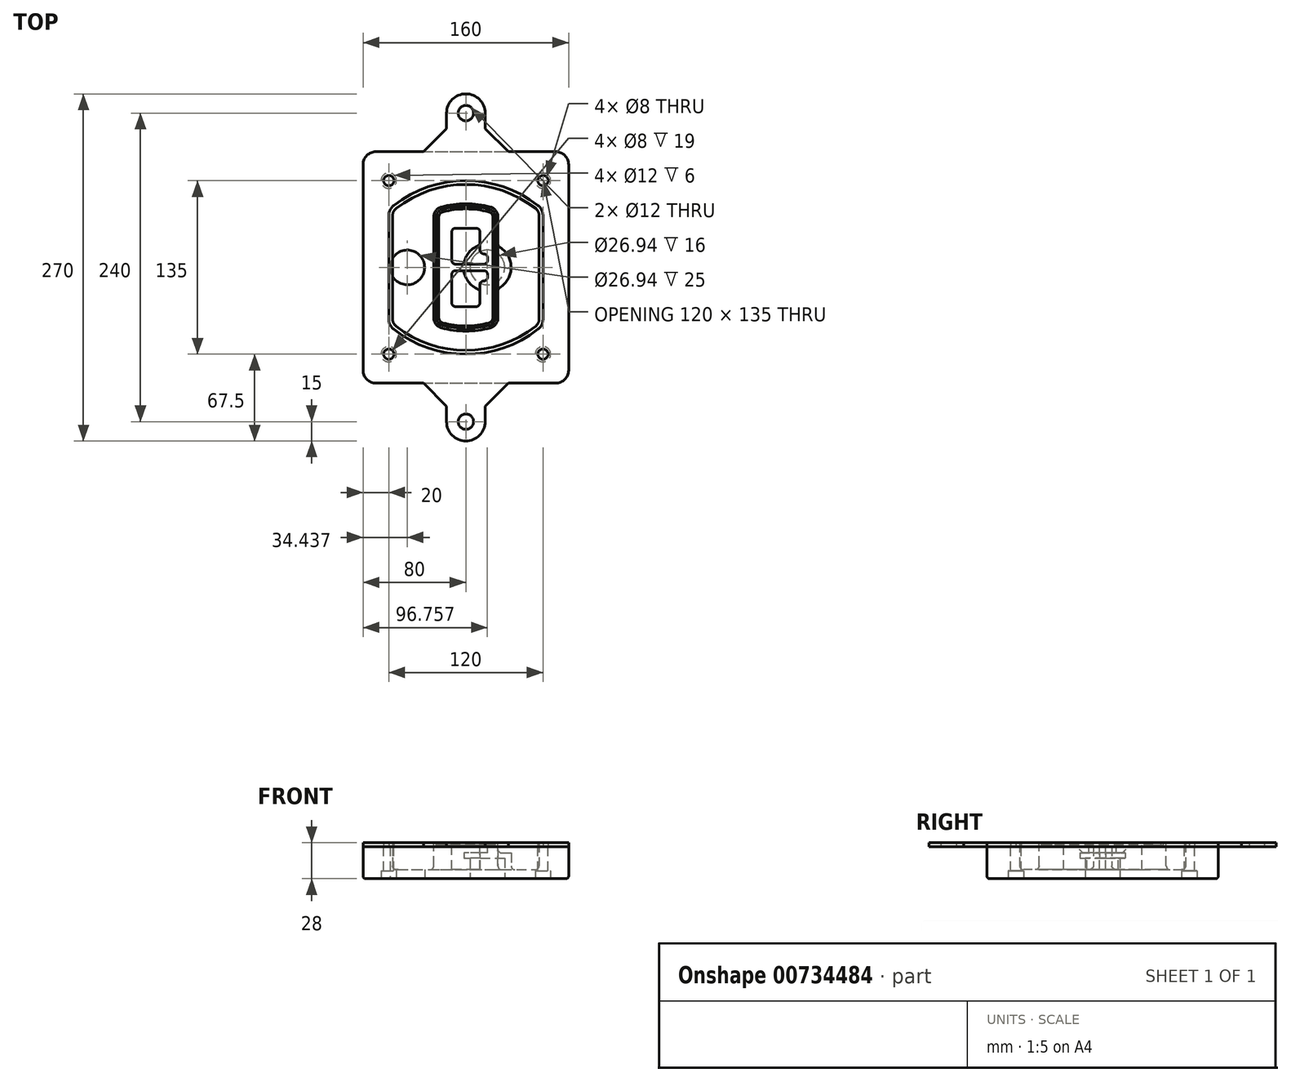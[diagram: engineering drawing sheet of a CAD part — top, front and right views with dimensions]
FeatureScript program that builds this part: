
annotation { "Feature Type Name" : "Feature", "Feature Type Description" : "" }
export const myFeature = defineFeature(function(context is Context, id is Id, definition is map)
    precondition{}
    {
        {
            var Q0;
            Q0=qCreatedBy(makeId("Top.planeOp"),FACE);
            var sketch = newSketch(context, id + "F0", { "sketchPlane" : qUnion([Q0])});
            skPoint(sketch, "E0.rect.middle", {"position": v(0, 0) * mm});
            skLineSegment(sketch, "E1.bottom", {"start": v(-70, -90) * mm, "end": v(70, -90) * mm});
            skLineSegment(sketch, "E1.top", {"start": v(-70, 90) * mm, "end": v(70, 90) * mm});
            skLineSegment(sketch, "E1.left", {"start": v(-80, -80) * mm, "end": v(-80, 80) * mm});
            skLineSegment(sketch, "E1.right", {"start": v(80, -80) * mm, "end": v(80, 80) * mm});
            skLineSegment(sketch, "E2", {"start": v(-80, 90) * mm, "end": v(80, -90) * mm, "construction": true});
            skLineSegment(sketch, "E3", {"start": v(80, 90) * mm, "end": v(-80, -90) * mm, "construction": true});
            skCircle(sketch, "E4", {"center": v(-60, 67.5) * mm, "radius": 4 * mm});
            skCircle(sketch, "E5", {"center": v(60, 67.5) * mm, "radius": 4 * mm});
            skCircle(sketch, "E6", {"center": v(60, -67.5) * mm, "radius": 4 * mm});
            skCircle(sketch, "E7", {"center": v(-60, -67.5) * mm, "radius": 4 * mm});
            skLineSegment(sketch, "E8", {"start": v(-60, 67.5) * mm, "end": v(60, 67.5) * mm, "construction": true});
            skLineSegment(sketch, "E9", {"start": v(60, 67.5) * mm, "end": v(60, -67.5) * mm, "construction": true});
            skLineSegment(sketch, "E10", {"start": v(60, -67.5) * mm, "end": v(-60, -67.5) * mm, "construction": true});
            skLineSegment(sketch, "E11", {"start": v(-60, -67.5) * mm, "end": v(-60, 67.5) * mm, "construction": true});
            skLineSegment(sketch, "E12", {"start": v(-60, 40.3) * mm, "end": v(-60, -40.3) * mm});
            skLineSegment(sketch, "E13", {"start": v(60, 40.3) * mm, "end": v(60, -40.3) * mm});
            skArc(sketch, "E14", {"start": v(56.15, 48.18) * mm, "mid": v(0, 67.5) * mm, "end": v(-56.15, 48.18) * mm});
            skArc(sketch, "E15", {"start": v(-56.15, -48.18) * mm, "mid": v(0, -67.5) * mm, "end": v(56.15, -48.18) * mm});
            skLineSegment(sketch, "E16", {"start": v(-60, 0) * mm, "end": v(60, 0) * mm, "construction": true});
            skPoint(sketch, "E17.visualSharp", {"position": v(-60, -45) * mm});
            skArc(sketch, "E17.filletArc", {"start": v(-60, -40.3) * mm, "mid": v(-58.99, -44.68) * mm, "end": v(-56.15, -48.18) * mm});
            skPoint(sketch, "E18.visualSharp", {"position": v(-60, 45) * mm});
            skArc(sketch, "E18.filletArc", {"start": v(-56.15, 48.18) * mm, "mid": v(-58.99, 44.68) * mm, "end": v(-60, 40.3) * mm});
            skPoint(sketch, "E19.visualSharp", {"position": v(60, 45) * mm});
            skArc(sketch, "E19.filletArc", {"start": v(60, 40.3) * mm, "mid": v(58.99, 44.68) * mm, "end": v(56.15, 48.18) * mm});
            skPoint(sketch, "E20.visualSharp", {"position": v(60, -45) * mm});
            skArc(sketch, "E20.filletArc", {"start": v(56.15, -48.18) * mm, "mid": v(58.99, -44.68) * mm, "end": v(60, -40.3) * mm});
            skPoint(sketch, "E21.visualSharp", {"position": v(-80, 90) * mm});
            skArc(sketch, "E21.filletArc", {"start": v(-70, 90) * mm, "mid": v(-77.07, 87.07) * mm, "end": v(-80, 80) * mm});
            skPoint(sketch, "E22.visualSharp", {"position": v(80, 90) * mm});
            skArc(sketch, "E22.filletArc", {"start": v(80, 80) * mm, "mid": v(77.07, 87.07) * mm, "end": v(70, 90) * mm});
            skPoint(sketch, "E23.visualSharp", {"position": v(80, -90) * mm});
            skArc(sketch, "E23.filletArc", {"start": v(70, -90) * mm, "mid": v(77.07, -87.07) * mm, "end": v(80, -80) * mm});
            skPoint(sketch, "E24.visualSharp", {"position": v(-80, -90) * mm});
            skArc(sketch, "E24.filletArc", {"start": v(-80, -80) * mm, "mid": v(-77.07, -87.07) * mm, "end": v(-70, -90) * mm});
            skArc(sketch, "E25.0", {"start": v(57, 40.3) * mm, "mid": v(56.3, 43.36) * mm, "end": v(54.3, 45.81) * mm});
            skLineSegment(sketch, "E25.1", {"start": v(57, 40.3) * mm, "end": v(57, -40.3) * mm});
            skArc(sketch, "E25.2", {"start": v(54.3, -45.81) * mm, "mid": v(56.3, -43.36) * mm, "end": v(57, -40.3) * mm});
            skArc(sketch, "E25.3", {"start": v(-54.3, -45.81) * mm, "mid": v(0, -64.5) * mm, "end": v(54.3, -45.81) * mm});
            skArc(sketch, "E25.4", {"start": v(-57, -40.3) * mm, "mid": v(-56.3, -43.36) * mm, "end": v(-54.3, -45.81) * mm});
            skArc(sketch, "E25.5", {"start": v(54.3, 45.81) * mm, "mid": v(0, 64.5) * mm, "end": v(-54.3, 45.81) * mm});
            skLineSegment(sketch, "E25.6", {"start": v(-57, 40.3) * mm, "end": v(-57, -40.3) * mm});
            skArc(sketch, "E25.7", {"start": v(-54.3, 45.81) * mm, "mid": v(-56.3, 43.36) * mm, "end": v(-57, 40.3) * mm});
            skArc(sketch, "E26.0", {"start": v(-58.62, 51.33) * mm, "mid": v(-62.58, 46.43) * mm, "end": v(-64, 40.3) * mm});
            skArc(sketch, "E26.1", {"start": v(58.62, 51.33) * mm, "mid": v(0, 71.5) * mm, "end": v(-58.62, 51.33) * mm});
            skArc(sketch, "E26.2", {"start": v(64, 40.3) * mm, "mid": v(62.58, 46.43) * mm, "end": v(58.62, 51.33) * mm});
            skLineSegment(sketch, "E26.3", {"start": v(64, 40.3) * mm, "end": v(64, -40.3) * mm});
            skArc(sketch, "E26.4", {"start": v(58.62, -51.33) * mm, "mid": v(62.58, -46.43) * mm, "end": v(64, -40.3) * mm});
            skLineSegment(sketch, "E26.5", {"start": v(-64, 40.3) * mm, "end": v(-64, -40.3) * mm});
            skArc(sketch, "E26.6", {"start": v(-58.62, -51.33) * mm, "mid": v(0, -71.5) * mm, "end": v(58.62, -51.33) * mm});
            skArc(sketch, "E26.7", {"start": v(-64, -40.3) * mm, "mid": v(-62.58, -46.43) * mm, "end": v(-58.62, -51.33) * mm});
            skSolve(sketch);
        }
        {
            var Q0;
            Q0=makeQuery(id+"F0.imprint","IMPRINT",FACE,{"disambiguationData":[TD([[makeQuery(id+"F0.imprint","IMPRINT",EDGE,{"derivedFrom":sQuery(id+"F0.wireOp",EDGE,"E1.bottom")}),1.0]])]});
            var Q1;
            Q1=makeQuery(id+"F0.imprint","IMPRINT",FACE,{"disambiguationData":[TD([[makeQuery(id+"F0.imprint","IMPRINT",EDGE,{"derivedFrom":sQuery(id+"F0.wireOp",EDGE,"E12")}),1.0]])]});
            var Q2;
            Q2=makeQuery(id+"F0.imprint","IMPRINT",FACE,{"disambiguationData":[TD([[makeQuery(id+"F0.imprint","IMPRINT",EDGE,{"derivedFrom":sQuery(id+"F0.wireOp",EDGE,"E25.0")}),1.0]])]});
            var Q3;
            Q3=makeQuery(id+"F0.imprint","IMPRINT",FACE,{"disambiguationData":[TD([[makeQuery(id+"F0.imprint","IMPRINT",EDGE,{"derivedFrom":sQuery(id+"F0.wireOp",EDGE,"E12")}),-1.0]])]});
            extrude(context, id + "F1", {"entities" : qUnion([Q0, Q1, Q2, Q3]), "oppositeDirection" : true, "depth" : 25 * mm});
        }
        {
            var Q0;
            Q0=makeQuery(id+"F0.imprint","IMPRINT",FACE,{"disambiguationData":[TD([[makeQuery(id+"F0.imprint","IMPRINT",EDGE,{"derivedFrom":sQuery(id+"F0.wireOp",EDGE,"E12")}),1.0]])]});
            extrude(context, id + "F2", {"entities" : qUnion([Q0]), "operationType" : NewBodyOperationType.ADD, "depth" : 3 * mm});
        }
        {
            var Q0;
            Q0=makeQuery(id+"F0.imprint","IMPRINT",FACE,{"disambiguationData":[TD([[makeQuery(id+"F0.imprint","IMPRINT",EDGE,{"derivedFrom":sQuery(id+"F0.wireOp",EDGE,"E25.0")}),1.0]])]});
            extrude(context, id + "F3", {"entities" : qUnion([Q0]), "operationType" : NewBodyOperationType.REMOVE, "oppositeDirection" : true, "depth" : 18 * mm});
        }
        {
            var Q0;
            Q0=makeQuery(id+"F2.opExtrude","CAP_FACE",FACE,{"disambiguationData":[OSD([sQuery(id+"F0.wireOp",EDGE,"E12"),sQuery(id+"F0.wireOp",EDGE,"E13"),sQuery(id+"F0.wireOp",EDGE,"E14"),sQuery(id+"F0.wireOp",EDGE,"E15"),sQuery(id+"F0.wireOp",EDGE,"E17.filletArc"),sQuery(id+"F0.wireOp",EDGE,"E18.filletArc"),sQuery(id+"F0.wireOp",EDGE,"E19.filletArc"),sQuery(id+"F0.wireOp",EDGE,"E20.filletArc"),sQuery(id+"F0.wireOp",EDGE,"E25.0"),sQuery(id+"F0.wireOp",EDGE,"E25.1"),sQuery(id+"F0.wireOp",EDGE,"E25.2"),sQuery(id+"F0.wireOp",EDGE,"E25.3"),sQuery(id+"F0.wireOp",EDGE,"E25.4"),sQuery(id+"F0.wireOp",EDGE,"E25.5"),sQuery(id+"F0.wireOp",EDGE,"E25.6"),sQuery(id+"F0.wireOp",EDGE,"E25.7")])],"isStart":false});
            var sketch = newSketch(context, id + "F4", { "sketchPlane" : qUnion([Q0])});
            skArc(sketch, "E27.0", {"start": v(-19.08, -46.97) * mm, "mid": v(0, -49.5) * mm, "end": v(19.08, -46.97) * mm});
            skArc(sketch, "E28.0", {"start": v(19.08, 46.97) * mm, "mid": v(0, 49.5) * mm, "end": v(-19.08, 46.97) * mm});
            skLineSegment(sketch, "E29", {"start": v(-25, 39.25) * mm, "end": v(-25, -39.25) * mm});
            skLineSegment(sketch, "E30", {"start": v(25, 39.25) * mm, "end": v(25, -39.25) * mm});
            skLineSegment(sketch, "E31", {"start": v(-25, 45.1) * mm, "end": v(25, 45.1) * mm, "construction": true});
            skLineSegment(sketch, "E32", {"start": v(-25, -45.1) * mm, "end": v(25, -45.1) * mm, "construction": true});
            skPoint(sketch, "E33.visualSharp", {"position": v(-25, 45.1) * mm});
            skArc(sketch, "E33.filletArc", {"start": v(-19.08, 46.97) * mm, "mid": v(-23.35, 44.11) * mm, "end": v(-25, 39.25) * mm});
            skPoint(sketch, "E34.visualSharp", {"position": v(25, 45.1) * mm});
            skArc(sketch, "E34.filletArc", {"start": v(25, 39.25) * mm, "mid": v(23.35, 44.11) * mm, "end": v(19.08, 46.97) * mm});
            skPoint(sketch, "E35.visualSharp", {"position": v(25, -45.1) * mm});
            skArc(sketch, "E35.filletArc", {"start": v(19.08, -46.97) * mm, "mid": v(23.35, -44.11) * mm, "end": v(25, -39.25) * mm});
            skPoint(sketch, "E36.visualSharp", {"position": v(-25, -45.1) * mm});
            skArc(sketch, "E36.filletArc", {"start": v(-25, -39.25) * mm, "mid": v(-23.35, -44.11) * mm, "end": v(-19.08, -46.97) * mm});
            skArc(sketch, "E37.0", {"start": v(54.3, 45.81) * mm, "mid": v(0, 64.5) * mm, "end": v(-54.3, 45.81) * mm});
            skArc(sketch, "E37.1", {"start": v(-54.3, 45.81) * mm, "mid": v(-56.3, 43.36) * mm, "end": v(-57, 40.3) * mm});
            skLineSegment(sketch, "E37.2", {"start": v(-57, 40.3) * mm, "end": v(-57, -40.3) * mm});
            skArc(sketch, "E37.3", {"start": v(-57, -40.3) * mm, "mid": v(-56.3, -43.36) * mm, "end": v(-54.3, -45.81) * mm});
            skArc(sketch, "E37.4", {"start": v(-54.3, -45.81) * mm, "mid": v(0, -64.5) * mm, "end": v(54.3, -45.81) * mm});
            skArc(sketch, "E37.5", {"start": v(54.3, -45.81) * mm, "mid": v(56.3, -43.36) * mm, "end": v(57, -40.3) * mm});
            skLineSegment(sketch, "E37.6", {"start": v(57, 40.3) * mm, "end": v(57, -40.3) * mm});
            skArc(sketch, "E37.7", {"start": v(57, 40.3) * mm, "mid": v(56.3, 43.36) * mm, "end": v(54.3, 45.81) * mm});
            skLineSegment(sketch, "E38.0", {"start": v(23, 39.25) * mm, "end": v(23, -39.25) * mm});
            skArc(sketch, "E38.1", {"start": v(18.56, -45.04) * mm, "mid": v(21.76, -42.9) * mm, "end": v(23, -39.25) * mm});
            skArc(sketch, "E38.2", {"start": v(-18.56, -45.04) * mm, "mid": v(0, -47.5) * mm, "end": v(18.56, -45.04) * mm});
            skArc(sketch, "E38.3", {"start": v(-23, -39.25) * mm, "mid": v(-21.76, -42.9) * mm, "end": v(-18.56, -45.04) * mm});
            skLineSegment(sketch, "E38.4", {"start": v(-23, 39.25) * mm, "end": v(-23, -39.25) * mm});
            skArc(sketch, "E38.5", {"start": v(23, 39.25) * mm, "mid": v(21.76, 42.9) * mm, "end": v(18.56, 45.04) * mm});
            skArc(sketch, "E38.6", {"start": v(-18.56, 45.04) * mm, "mid": v(-21.76, 42.9) * mm, "end": v(-23, 39.25) * mm});
            skArc(sketch, "E38.7", {"start": v(18.56, 45.04) * mm, "mid": v(0, 47.5) * mm, "end": v(-18.56, 45.04) * mm});
            skArc(sketch, "E39.0", {"start": v(21, 39.25) * mm, "mid": v(20.18, 41.68) * mm, "end": v(18.04, 43.1) * mm});
            skLineSegment(sketch, "E39.1", {"start": v(21, 39.25) * mm, "end": v(21, -39.25) * mm});
            skArc(sketch, "E39.2", {"start": v(18.04, -43.1) * mm, "mid": v(20.18, -41.68) * mm, "end": v(21, -39.25) * mm});
            skArc(sketch, "E39.3", {"start": v(-18.04, -43.1) * mm, "mid": v(0, -45.5) * mm, "end": v(18.04, -43.1) * mm});
            skArc(sketch, "E39.4", {"start": v(-21, -39.25) * mm, "mid": v(-20.18, -41.68) * mm, "end": v(-18.04, -43.1) * mm});
            skArc(sketch, "E39.5", {"start": v(18.04, 43.1) * mm, "mid": v(0, 45.5) * mm, "end": v(-18.04, 43.1) * mm});
            skLineSegment(sketch, "E39.6", {"start": v(-21, 39.25) * mm, "end": v(-21, -39.25) * mm});
            skArc(sketch, "E39.7", {"start": v(-18.04, 43.1) * mm, "mid": v(-20.18, 41.68) * mm, "end": v(-21, 39.25) * mm});
            skLineSegment(sketch, "E40", {"start": v(-25, 0) * mm, "end": v(25, 0) * mm, "construction": true});
            skLineSegment(sketch, "E41", {"start": v(-11, 5.5) * mm, "end": v(-11, 27.5) * mm});
            skLineSegment(sketch, "E42", {"start": v(-8, 30.5) * mm, "end": v(8, 30.5) * mm});
            skLineSegment(sketch, "E43", {"start": v(11, 27.5) * mm, "end": v(11, 13.5) * mm});
            skLineSegment(sketch, "E44", {"start": v(14, 10.5) * mm, "end": v(14, 10.5) * mm});
            skLineSegment(sketch, "E45", {"start": v(17, 7.5) * mm, "end": v(17, 5.5) * mm});
            skLineSegment(sketch, "E46", {"start": v(14, 2.5) * mm, "end": v(-8, 2.5) * mm});
            skPoint(sketch, "E47.visualSharp", {"position": v(-11, 30.5) * mm});
            skArc(sketch, "E47.filletArc", {"start": v(-8, 30.5) * mm, "mid": v(-10.12, 29.62) * mm, "end": v(-11, 27.5) * mm});
            skPoint(sketch, "E48.visualSharp", {"position": v(11, 30.5) * mm});
            skArc(sketch, "E48.filletArc", {"start": v(11, 27.5) * mm, "mid": v(10.12, 29.62) * mm, "end": v(8, 30.5) * mm});
            skPoint(sketch, "E49.visualSharp", {"position": v(11, 10.5) * mm});
            skArc(sketch, "E49.filletArc", {"start": v(11, 13.5) * mm, "mid": v(11.88, 11.38) * mm, "end": v(14, 10.5) * mm});
            skPoint(sketch, "E50.visualSharp", {"position": v(17, 10.5) * mm});
            skArc(sketch, "E50.filletArc", {"start": v(17, 7.5) * mm, "mid": v(16.12, 9.62) * mm, "end": v(14, 10.5) * mm});
            skPoint(sketch, "E51.visualSharp", {"position": v(17, 2.5) * mm});
            skArc(sketch, "E51.filletArc", {"start": v(14, 2.5) * mm, "mid": v(16.12, 3.38) * mm, "end": v(17, 5.5) * mm});
            skPoint(sketch, "E52.visualSharp", {"position": v(-11, 2.5) * mm});
            skArc(sketch, "E52.filletArc", {"start": v(-11, 5.5) * mm, "mid": v(-10.12, 3.38) * mm, "end": v(-8, 2.5) * mm});
            skLineSegment(sketch, "E53.0.MirrorCS", {"start": v(14, -2.5) * mm, "end": v(-8, -2.5) * mm});
            skArc(sketch, "E54.0.MirrorCS", {"start": v(-11, -5.5) * mm, "mid": v(-10.12, -3.38) * mm, "end": v(-8, -2.5) * mm});
            skLineSegment(sketch, "E55.0.MirrorCS", {"start": v(-11, -5.5) * mm, "end": v(-11, -27.5) * mm});
            skArc(sketch, "E56.0.MirrorCS", {"start": v(-8, -30.5) * mm, "mid": v(-10.12, -29.62) * mm, "end": v(-11, -27.5) * mm});
            skLineSegment(sketch, "E57.0.MirrorCS", {"start": v(-8, -30.5) * mm, "end": v(8, -30.5) * mm});
            skArc(sketch, "E58.0.MirrorCS", {"start": v(11, -27.5) * mm, "mid": v(10.12, -29.62) * mm, "end": v(8, -30.5) * mm});
            skLineSegment(sketch, "E59.0.MirrorCS", {"start": v(11, -27.5) * mm, "end": v(11, -13.5) * mm});
            skArc(sketch, "E60.0.MirrorCS", {"start": v(11, -13.5) * mm, "mid": v(11.88, -11.38) * mm, "end": v(14, -10.5) * mm});
            skArc(sketch, "E61.0.MirrorCS", {"start": v(17, -7.5) * mm, "mid": v(16.12, -9.62) * mm, "end": v(14, -10.5) * mm});
            skLineSegment(sketch, "E62.0.MirrorCS", {"start": v(17, -7.5) * mm, "end": v(17, -5.5) * mm});
            skArc(sketch, "E63.0.MirrorCS", {"start": v(14, -2.5) * mm, "mid": v(16.12, -3.38) * mm, "end": v(17, -5.5) * mm});
            skSolve(sketch);
        }
        {
            var Q0;
            Q0=makeQuery(id+"F4.imprint","IMPRINT",FACE,{"disambiguationData":[TD([[makeQuery(id+"F4.imprint","IMPRINT",EDGE,{"derivedFrom":sQuery(id+"F4.wireOp",EDGE,"E27.0")}),1.0]])]});
            var Q1;
            Q1=makeQuery(id+"F4.imprint","IMPRINT",FACE,{"disambiguationData":[TD([[makeQuery(id+"F4.imprint","IMPRINT",EDGE,{"derivedFrom":sQuery(id+"F4.wireOp",EDGE,"E38.0")}),-1.0]])]});
            var Q2;
            Q2=makeQuery(id+"F4.imprint","IMPRINT",FACE,{"disambiguationData":[TD([[makeQuery(id+"F4.imprint","IMPRINT",EDGE,{"derivedFrom":sQuery(id+"F4.wireOp",EDGE,"E39.0")}),1.0]])]});
            extrude(context, id + "F5", {"entities" : qUnion([Q0, Q1, Q2]), "operationType" : NewBodyOperationType.ADD, "endBound" : BoundingType.UP_TO_NEXT, "oppositeDirection" : true, "depth" : 25 * mm});
        }
        {
            var Q0;
            Q0=makeQuery(id+"F4.imprint","IMPRINT",FACE,{"disambiguationData":[TD([[makeQuery(id+"F4.imprint","IMPRINT",EDGE,{"derivedFrom":sQuery(id+"F4.wireOp",EDGE,"E38.0")}),-1.0]])]});
            extrude(context, id + "F6", {"entities" : qUnion([Q0]), "operationType" : NewBodyOperationType.REMOVE, "oppositeDirection" : true, "depth" : 2 * mm});
        }
        {
            var Q0;
            Q0=makeQuery(id+"F1.opExtrude","CAP_FACE",FACE,{"disambiguationData":[OSD([sQuery(id+"F0.wireOp",EDGE,"E1.bottom"),sQuery(id+"F0.wireOp",EDGE,"E1.top"),sQuery(id+"F0.wireOp",EDGE,"E1.left"),sQuery(id+"F0.wireOp",EDGE,"E1.right"),sQuery(id+"F0.wireOp",EDGE,"E4"),sQuery(id+"F0.wireOp",EDGE,"E5"),sQuery(id+"F0.wireOp",EDGE,"E6"),sQuery(id+"F0.wireOp",EDGE,"E7"),sQuery(id+"F0.wireOp",EDGE,"E21.filletArc"),sQuery(id+"F0.wireOp",EDGE,"E22.filletArc"),sQuery(id+"F0.wireOp",EDGE,"E23.filletArc"),sQuery(id+"F0.wireOp",EDGE,"E24.filletArc")])],"isStart":false});
            var sketch = newSketch(context, id + "F7", { "sketchPlane" : qUnion([Q0])});
            skCircle(sketch, "E64", {"center": v(16.76, 0) * mm, "radius": 13.47 * mm});
            skCircle(sketch, "E65", {"center": v(-45.56, 0) * mm, "radius": 13.47 * mm});
            skLineSegment(sketch, "E66", {"start": v(80, 0) * mm, "end": v(-80, 0) * mm});
            skCircle(sketch, "E67", {"center": v(16.76, 0) * mm, "radius": 18.47 * mm});
            skCircle(sketch, "E68", {"center": v(60, -67.5) * mm, "radius": 6 * mm});
            skCircle(sketch, "E69", {"center": v(-60, -67.5) * mm, "radius": 6 * mm});
            skCircle(sketch, "E70", {"center": v(-60, 67.5) * mm, "radius": 6 * mm});
            skCircle(sketch, "E71", {"center": v(60, 67.5) * mm, "radius": 6 * mm});
            skSolve(sketch);
        }
        {
            var Q0;
            {var subQ1=sQuery(id+"F7.wireOp",EDGE,"E66");var subQ4=sQuery(id+"F7.wireOp",EDGE,"E64");var subQ6=makeQuery(id+"F7.imprint","INTERSECT",VERTEX,{"disambiguationData":[OD(0.0)],"derivedFrom":[subQ4,subQ1]});Q0=makeQuery(id+"F7.imprint","IMPRINT",FACE,{"disambiguationData":[TD([[makeQuery(id+"F7.imprint","IMPRINT",EDGE,{"disambiguationData":[TD([[subQ6,-1.0]])],"derivedFrom":subQ4}),-1.0]])]});}
            var Q1;
            {var subQ0=sQuery(id+"F7.wireOp",EDGE,"E66");var subQ1=sQuery(id+"F7.wireOp",EDGE,"E64");var subQ3=makeQuery(id+"F7.imprint","INTERSECT",VERTEX,{"disambiguationData":[OD(0.0)],"derivedFrom":[subQ1,subQ0]});Q1=makeQuery(id+"F7.imprint","IMPRINT",FACE,{"disambiguationData":[TD([[makeQuery(id+"F7.imprint","IMPRINT",EDGE,{"disambiguationData":[TD([[subQ3,-1.0]])],"derivedFrom":subQ1}),1.0]])]});}
            var Q2;
            {var subQ0=sQuery(id+"F7.wireOp",EDGE,"E66");var subQ1=sQuery(id+"F7.wireOp",EDGE,"E64");var subQ3=makeQuery(id+"F7.imprint","INTERSECT",VERTEX,{"disambiguationData":[OD(0.0)],"derivedFrom":[subQ1,subQ0]});Q2=makeQuery(id+"F7.imprint","IMPRINT",FACE,{"disambiguationData":[TD([[makeQuery(id+"F7.imprint","IMPRINT",EDGE,{"disambiguationData":[TD([[subQ3,1.0]])],"derivedFrom":subQ1}),1.0]])]});}
            var Q3;
            {var subQ1=sQuery(id+"F7.wireOp",EDGE,"E66");var subQ4=sQuery(id+"F7.wireOp",EDGE,"E64");var subQ6=makeQuery(id+"F7.imprint","INTERSECT",VERTEX,{"disambiguationData":[OD(0.0)],"derivedFrom":[subQ4,subQ1]});Q3=makeQuery(id+"F7.imprint","IMPRINT",FACE,{"disambiguationData":[TD([[makeQuery(id+"F7.imprint","IMPRINT",EDGE,{"disambiguationData":[TD([[subQ6,1.0]])],"derivedFrom":subQ4}),-1.0]])]});}
            extrude(context, id + "F8", {"entities" : qUnion([Q0, Q1, Q2, Q3]), "operationType" : NewBodyOperationType.ADD, "oppositeDirection" : true, "depth" : 20 * mm});
        }
        {
            var Q0;
            {var subQ0=sQuery(id+"F7.wireOp",EDGE,"E66");var subQ1=sQuery(id+"F7.wireOp",EDGE,"E64");var subQ3=makeQuery(id+"F7.imprint","INTERSECT",VERTEX,{"disambiguationData":[OD(0.0)],"derivedFrom":[subQ1,subQ0]});Q0=makeQuery(id+"F7.imprint","IMPRINT",FACE,{"disambiguationData":[TD([[makeQuery(id+"F7.imprint","IMPRINT",EDGE,{"disambiguationData":[TD([[subQ3,-1.0]])],"derivedFrom":subQ1}),1.0]])]});}
            var Q1;
            {var subQ0=sQuery(id+"F7.wireOp",EDGE,"E66");var subQ1=sQuery(id+"F7.wireOp",EDGE,"E64");var subQ3=makeQuery(id+"F7.imprint","INTERSECT",VERTEX,{"disambiguationData":[OD(0.0)],"derivedFrom":[subQ1,subQ0]});Q1=makeQuery(id+"F7.imprint","IMPRINT",FACE,{"disambiguationData":[TD([[makeQuery(id+"F7.imprint","IMPRINT",EDGE,{"disambiguationData":[TD([[subQ3,1.0]])],"derivedFrom":subQ1}),1.0]])]});}
            extrude(context, id + "F9", {"entities" : qUnion([Q0, Q1]), "operationType" : NewBodyOperationType.REMOVE, "oppositeDirection" : true, "depth" : 16 * mm});
        }
        {
            var Q0;
            {var subQ0=sQuery(id+"F7.wireOp",EDGE,"E66");var subQ1=sQuery(id+"F7.wireOp",EDGE,"E65");var subQ3=makeQuery(id+"F7.imprint","INTERSECT",VERTEX,{"disambiguationData":[OD(0.0)],"derivedFrom":[subQ1,subQ0]});Q0=makeQuery(id+"F7.imprint","IMPRINT",FACE,{"disambiguationData":[TD([[makeQuery(id+"F7.imprint","IMPRINT",EDGE,{"disambiguationData":[TD([[subQ3,-1.0]])],"derivedFrom":subQ1}),1.0]])]});}
            var Q1;
            {var subQ0=sQuery(id+"F7.wireOp",EDGE,"E66");var subQ1=sQuery(id+"F7.wireOp",EDGE,"E65");var subQ3=makeQuery(id+"F7.imprint","INTERSECT",VERTEX,{"disambiguationData":[OD(0.0)],"derivedFrom":[subQ1,subQ0]});Q1=makeQuery(id+"F7.imprint","IMPRINT",FACE,{"disambiguationData":[TD([[makeQuery(id+"F7.imprint","IMPRINT",EDGE,{"disambiguationData":[TD([[subQ3,1.0]])],"derivedFrom":subQ1}),1.0]])]});}
            extrude(context, id + "F10", {"entities" : qUnion([Q0, Q1]), "operationType" : NewBodyOperationType.REMOVE, "oppositeDirection" : true, "depth" : 25 * mm});
        }
        {
            var Q0;
            Q0=makeQuery(id+"F7.imprint","IMPRINT",FACE,{"disambiguationData":[TD([[makeQuery(id+"F7.imprint","IMPRINT",EDGE,{"derivedFrom":sQuery(id+"F7.wireOp",EDGE,"E68")}),1.0]])]});
            var Q1;
            Q1=makeQuery(id+"F7.imprint","IMPRINT",FACE,{"disambiguationData":[TD([[makeQuery(id+"F7.imprint","IMPRINT",EDGE,{"derivedFrom":makeQuery(id+"F1.opExtrude","CAP_EDGE",EDGE,{"disambiguationData":[OSD([sQuery(id+"F0.wireOp",EDGE,"E5")])],"isStart":false})}),-1.0]])]});
            var Q2;
            Q2=makeQuery(id+"F7.imprint","IMPRINT",FACE,{"disambiguationData":[TD([[makeQuery(id+"F7.imprint","IMPRINT",EDGE,{"derivedFrom":sQuery(id+"F7.wireOp",EDGE,"E69")}),1.0]])]});
            var Q3;
            Q3=makeQuery(id+"F7.imprint","IMPRINT",FACE,{"disambiguationData":[TD([[makeQuery(id+"F7.imprint","IMPRINT",EDGE,{"derivedFrom":makeQuery(id+"F1.opExtrude","CAP_EDGE",EDGE,{"disambiguationData":[OSD([sQuery(id+"F0.wireOp",EDGE,"E4")])],"isStart":false})}),-1.0]])]});
            var Q4;
            Q4=makeQuery(id+"F7.imprint","IMPRINT",FACE,{"disambiguationData":[TD([[makeQuery(id+"F7.imprint","IMPRINT",EDGE,{"derivedFrom":sQuery(id+"F7.wireOp",EDGE,"E70")}),1.0]])]});
            var Q5;
            Q5=makeQuery(id+"F7.imprint","IMPRINT",FACE,{"disambiguationData":[TD([[makeQuery(id+"F7.imprint","IMPRINT",EDGE,{"derivedFrom":makeQuery(id+"F1.opExtrude","CAP_EDGE",EDGE,{"disambiguationData":[OSD([sQuery(id+"F0.wireOp",EDGE,"E7")])],"isStart":false})}),-1.0]])]});
            var Q6;
            Q6=makeQuery(id+"F7.imprint","IMPRINT",FACE,{"disambiguationData":[TD([[makeQuery(id+"F7.imprint","IMPRINT",EDGE,{"derivedFrom":sQuery(id+"F7.wireOp",EDGE,"E71")}),1.0]])]});
            var Q7;
            Q7=makeQuery(id+"F7.imprint","IMPRINT",FACE,{"disambiguationData":[TD([[makeQuery(id+"F7.imprint","IMPRINT",EDGE,{"derivedFrom":makeQuery(id+"F1.opExtrude","CAP_EDGE",EDGE,{"disambiguationData":[OSD([sQuery(id+"F0.wireOp",EDGE,"E6")])],"isStart":false})}),-1.0]])]});
            extrude(context, id + "F11", {"entities" : qUnion([Q0, Q1, Q2, Q3, Q4, Q5, Q6, Q7]), "operationType" : NewBodyOperationType.REMOVE, "oppositeDirection" : true, "depth" : 6 * mm});
        }
        {
            var Q0;
            Q0=makeQuery(id+"F9.boolean.opBoolean","COPY",FACE,{"derivedFrom":makeQuery(id+"F9.opExtrude","CAP_FACE",FACE,{"disambiguationData":[OSD([sQuery(id+"F7.wireOp",EDGE,"E64")])],"isStart":false})});
            var sketch = newSketch(context, id + "F12", { "sketchPlane" : qUnion([Q0])});
            skArc(sketch, "E72.0", {"start": v(11, 17.55) * mm, "mid": v(2.57, 11.82) * mm, "end": v(-1.54, 2.5) * mm});
            skArc(sketch, "E72.1", {"start": v(-1.54, -2.5) * mm, "mid": v(2.57, -11.82) * mm, "end": v(11, -17.55) * mm});
            skLineSegment(sketch, "E73", {"start": v(-1.54, -2.5) * mm, "end": v(14, -2.5) * mm});
            skLineSegment(sketch, "E74.0", {"start": v(14, 2.5) * mm, "end": v(-1.54, 2.5) * mm});
            skArc(sketch, "E74.1", {"start": v(14, 2.5) * mm, "mid": v(16.12, 3.38) * mm, "end": v(17, 5.5) * mm});
            skLineSegment(sketch, "E74.2", {"start": v(17, 7.5) * mm, "end": v(17, 5.5) * mm});
            skArc(sketch, "E74.3", {"start": v(17, 7.5) * mm, "mid": v(16.12, 9.62) * mm, "end": v(14, 10.5) * mm});
            skArc(sketch, "E74.4", {"start": v(11, 13.5) * mm, "mid": v(11.88, 11.38) * mm, "end": v(14, 10.5) * mm});
            skLineSegment(sketch, "E74.5", {"start": v(11, 17.55) * mm, "end": v(11, 13.5) * mm});
            skLineSegment(sketch, "E74.7", {"start": v(14, -2.5) * mm, "end": v(-1.54, -2.5) * mm});
            skArc(sketch, "E74.8", {"start": v(14, -2.5) * mm, "mid": v(16.12, -3.38) * mm, "end": v(17, -5.5) * mm});
            skLineSegment(sketch, "E74.9", {"start": v(17, -7.5) * mm, "end": v(17, -5.5) * mm});
            skArc(sketch, "E74.10", {"start": v(17, -7.5) * mm, "mid": v(16.12, -9.62) * mm, "end": v(14, -10.5) * mm});
            skArc(sketch, "E74.11", {"start": v(11, -13.5) * mm, "mid": v(11.88, -11.38) * mm, "end": v(14, -10.5) * mm});
            skLineSegment(sketch, "E74.12", {"start": v(11, -17.55) * mm, "end": v(11, -13.5) * mm});
            skPoint(sketch, "E75.orphan", {"position": v(11, -27.5) * mm});
            skPoint(sketch, "E76.orphan", {"position": v(-8, -2.5) * mm});
            skPoint(sketch, "E77.orphan", {"position": v(-8, 2.5) * mm});
            skPoint(sketch, "E78.orphan", {"position": v(11, 27.5) * mm});
            skSolve(sketch);
        }
        {
            var Q0;
            {var subQ7=sQuery(id+"F12.wireOp",EDGE,"E72.0");var subQ14=sQuery(id+"F12.wireOp",EDGE,"E72.1");var subQ16=sQuery(id+"F12.wireOp",EDGE,"E74.1");var subQ18=sQuery(id+"F12.wireOp",EDGE,"E74.8");Q0=qUnion([makeQuery(id+"F12.imprint","IMPRINT",FACE,{"disambiguationData":[TD([[makeQuery(id+"F12.imprint","IMPRINT",EDGE,{"derivedFrom":subQ7}),1.0]])]}),makeQuery(id+"F12.imprint","IMPRINT",FACE,{"disambiguationData":[TD([[makeQuery(id+"F12.imprint","IMPRINT",EDGE,{"derivedFrom":subQ14}),1.0]])]}),makeQuery(id+"F12.imprint","IMPRINT",FACE,{"disambiguationData":[TD([[makeQuery(id+"F12.imprint","IMPRINT",EDGE,{"derivedFrom":subQ16}),1.0]])]}),makeQuery(id+"F12.imprint","IMPRINT",FACE,{"disambiguationData":[TD([[makeQuery(id+"F12.imprint","IMPRINT",EDGE,{"derivedFrom":subQ18}),-1.0]])]})]);}
            var Q1;
            Q1=makeQuery(id+"F5.boolean.opBoolean","SPLIT",FACE,{"disambiguationData":[TD([makeQuery(id+"F5.opExtrude","SWEPT_FACE",FACE,{"disambiguationData":[OSD([sQuery(id+"F4.wireOp",EDGE,"E41")])]})])],"derivedFrom":makeQuery(id+"F3.boolean.opBoolean","COPY",FACE,{"derivedFrom":makeQuery(id+"F3.opExtrude","CAP_FACE",FACE,{"disambiguationData":[OSD([sQuery(id+"F0.wireOp",EDGE,"E25.0"),sQuery(id+"F0.wireOp",EDGE,"E25.1"),sQuery(id+"F0.wireOp",EDGE,"E25.2"),sQuery(id+"F0.wireOp",EDGE,"E25.3"),sQuery(id+"F0.wireOp",EDGE,"E25.4"),sQuery(id+"F0.wireOp",EDGE,"E25.5"),sQuery(id+"F0.wireOp",EDGE,"E25.6"),sQuery(id+"F0.wireOp",EDGE,"E25.7")])],"isStart":false})})});
            extrude(context, id + "F13", {"entities" : qUnion([Q0]), "operationType" : NewBodyOperationType.REMOVE, "endBound" : BoundingType.UP_TO_SURFACE, "endBoundEntityFace" : qUnion([Q1]), "depth" : 25 * mm});
        }
        {
            var Q0;
            Q0=makeQuery(id+"F3.boolean.opBoolean","COPY",EDGE,{"derivedFrom":makeQuery(id+"F3.opExtrude","CAP_EDGE",EDGE,{"disambiguationData":[OSD([sQuery(id+"F0.wireOp",EDGE,"E25.6")])],"isStart":false})});
            var Q1;
            Q1=makeQuery(id+"F8.boolean.opBoolean","INTERSECT",EDGE,{"derivedFrom":[makeQuery(id+"F5.opExtrude","SWEPT_FACE",FACE,{"disambiguationData":[OSD([sQuery(id+"F4.wireOp",EDGE,"E30")])]}),makeQuery(id+"F8.opExtrude","CAP_FACE",FACE,{"disambiguationData":[OSD([sQuery(id+"F7.wireOp",EDGE,"E67")])],"isStart":false})]});
            var Q2;
            Q2=makeQuery(id+"F8.boolean.opBoolean","INTERSECT",EDGE,{"disambiguationData":[OD(1.0)],"derivedFrom":[makeQuery(id+"F5.opExtrude","SWEPT_FACE",FACE,{"disambiguationData":[OSD([sQuery(id+"F4.wireOp",EDGE,"E30")])]}),makeQuery(id+"F8.opExtrude","SWEPT_FACE",FACE,{"disambiguationData":[OSD([sQuery(id+"F7.wireOp",EDGE,"E67")])]})]});
            var Q3;
            {var subQ0=sQuery(id+"F4.wireOp",EDGE,"E30");Q3=makeQuery(id+"F8.boolean.opBoolean","SPLIT",EDGE,{"disambiguationData":[TD([makeQuery(id+"F5.opExtrude","SWEPT_FACE",FACE,{"disambiguationData":[OSD([sQuery(id+"F4.wireOp",EDGE,"E35.filletArc")])]})])],"derivedFrom":makeQuery(id+"F5.opExtrude","CAP_EDGE",EDGE,{"disambiguationData":[OSD([subQ0])],"isStart":false})});}
            var Q4;
            {var subQ0=sQuery(id+"F0.wireOp",EDGE,"E25.7");var subQ1=sQuery(id+"F0.wireOp",EDGE,"E25.1");var subQ2=sQuery(id+"F0.wireOp",EDGE,"E25.6");var subQ3=sQuery(id+"F0.wireOp",EDGE,"E25.5");var subQ4=sQuery(id+"F0.wireOp",EDGE,"E25.4");var subQ5=sQuery(id+"F0.wireOp",EDGE,"E25.0");var subQ6=sQuery(id+"F0.wireOp",EDGE,"E25.2");var subQ7=sQuery(id+"F0.wireOp",EDGE,"E25.3");Q4=makeQuery(id+"F8.boolean.opBoolean","INTERSECT",EDGE,{"derivedFrom":[makeQuery(id+"F5.boolean.opBoolean","SPLIT",FACE,{"disambiguationData":[TD([makeQuery(id+"F2.opExtrude","SWEPT_FACE",FACE,{"disambiguationData":[OSD([subQ5])]})])],"derivedFrom":makeQuery(id+"F3.boolean.opBoolean","COPY",FACE,{"derivedFrom":makeQuery(id+"F3.opExtrude","CAP_FACE",FACE,{"disambiguationData":[OSD([subQ5,subQ1,subQ6,subQ7,subQ4,subQ3,subQ2,subQ0])],"isStart":false})})}),makeQuery(id+"F8.opExtrude","SWEPT_FACE",FACE,{"disambiguationData":[OSD([sQuery(id+"F7.wireOp",EDGE,"E67")])]})]});}
            var Q5;
            Q5=makeQuery(id+"F8.boolean.opBoolean","INTERSECT",EDGE,{"disambiguationData":[OD(0.0)],"derivedFrom":[makeQuery(id+"F5.opExtrude","SWEPT_FACE",FACE,{"disambiguationData":[OSD([sQuery(id+"F4.wireOp",EDGE,"E30")])]}),makeQuery(id+"F8.opExtrude","SWEPT_FACE",FACE,{"disambiguationData":[OSD([sQuery(id+"F7.wireOp",EDGE,"E67")])]})]});
            fillet(context, id + "F14", {"entities" : qUnion([Q0, Q1, Q2, Q3, Q4, Q5]), "radius" : 3 * mm, "tangentPropagation" : true, "allowEdgeOverflow" : false});
        }
        {
            var Q0;
            Q0=makeQuery(id+"F1.opExtrude","CAP_EDGE",EDGE,{"disambiguationData":[OSD([sQuery(id+"F0.wireOp",EDGE,"E1.bottom")])],"isStart":false});
            fillet(context, id + "F15", {"entities" : qUnion([Q0]), "radius" : 2 * mm, "tangentPropagation" : true, "allowEdgeOverflow" : false});
        }
        {
            var Q0;
            {var subQ0=sQuery(id+"F0.wireOp",EDGE,"E21.filletArc");var subQ1=sQuery(id+"F0.wireOp",EDGE,"E7");var subQ2=sQuery(id+"F0.wireOp",EDGE,"E6");var subQ3=sQuery(id+"F0.wireOp",EDGE,"E5");var subQ4=sQuery(id+"F0.wireOp",EDGE,"E4");var subQ5=sQuery(id+"F0.wireOp",EDGE,"E22.filletArc");var subQ6=sQuery(id+"F0.wireOp",EDGE,"E1.bottom");var subQ7=sQuery(id+"F0.wireOp",EDGE,"E1.right");var subQ8=sQuery(id+"F0.wireOp",EDGE,"E1.top");var subQ9=sQuery(id+"F0.wireOp",EDGE,"E1.left");var subQ10=sQuery(id+"F0.wireOp",EDGE,"E23.filletArc");var subQ11=sQuery(id+"F0.wireOp",EDGE,"E24.filletArc");Q0=makeQuery(id+"F2.boolean.opBoolean","SPLIT",FACE,{"disambiguationData":[TD([makeQuery(id+"F1.opExtrude","SWEPT_FACE",FACE,{"disambiguationData":[OSD([subQ6])]})])],"derivedFrom":makeQuery(id+"F1.opExtrude","CAP_FACE",FACE,{"disambiguationData":[OSD([subQ6,subQ8,subQ9,subQ7,subQ4,subQ3,subQ2,subQ1,subQ0,subQ5,subQ10,subQ11])],"isStart":true})});}
            var sketch = newSketch(context, id + "F16", { "sketchPlane" : qUnion([Q0])});
            skLineSegment(sketch, "E79.0.0", {"start": v(70, 90) * mm, "end": v(-70, 90) * mm});
            skArc(sketch, "E79.0.1", {"start": v(-70, 90) * mm, "mid": v(-77.07, 87.07) * mm, "end": v(-80, 80) * mm});
            skLineSegment(sketch, "E79.0.2", {"start": v(-80, 80) * mm, "end": v(-80, -80) * mm});
            skArc(sketch, "E79.0.3", {"start": v(-80, -80) * mm, "mid": v(-77.07, -87.07) * mm, "end": v(-70, -90) * mm});
            skLineSegment(sketch, "E79.0.4", {"start": v(-70, -90) * mm, "end": v(70, -90) * mm});
            skArc(sketch, "E79.0.5", {"start": v(70, -90) * mm, "mid": v(77.07, -87.07) * mm, "end": v(80, -80) * mm});
            skLineSegment(sketch, "E79.0.6", {"start": v(80, -80) * mm, "end": v(80, 80) * mm});
            skArc(sketch, "E79.0.7", {"start": v(80, 80) * mm, "mid": v(77.07, 87.07) * mm, "end": v(70, 90) * mm});
            skCircle(sketch, "E80", {"center": v(0, 120) * mm, "radius": 6 * mm});
            skArc(sketch, "E81", {"start": v(-15, 120) * mm, "mid": v(0, 135) * mm, "end": v(15, 120) * mm});
            skLineSegment(sketch, "E82", {"start": v(-15, 120) * mm, "end": v(-15, 108) * mm});
            skLineSegment(sketch, "E83", {"start": v(-33, 90) * mm, "end": v(-15, 108) * mm});
            skLineSegment(sketch, "E84", {"start": v(0, 90) * mm, "end": v(0, 120) * mm, "construction": true});
            skLineSegment(sketch, "E85", {"start": v(15, 120) * mm, "end": v(15, 108) * mm});
            skLineSegment(sketch, "E86", {"start": v(15, 108) * mm, "end": v(33, 90) * mm});
            skLineSegment(sketch, "E87", {"start": v(-80, 0) * mm, "end": v(80, 0) * mm, "construction": true});
            skLineSegment(sketch, "E88.MirrorCS", {"start": v(-33, -90) * mm, "end": v(-15, -108) * mm});
            skLineSegment(sketch, "E89.MirrorCS", {"start": v(-15, -120) * mm, "end": v(-15, -108) * mm});
            skArc(sketch, "E90.MirrorCS", {"start": v(-15, -120) * mm, "mid": v(0, -135) * mm, "end": v(15, -120) * mm});
            skCircle(sketch, "E91.MirrorC", {"center": v(0, -120) * mm, "radius": 6 * mm});
            skLineSegment(sketch, "E92.MirrorCS", {"start": v(15, -120) * mm, "end": v(15, -108) * mm});
            skLineSegment(sketch, "E93.MirrorCS", {"start": v(15, -108) * mm, "end": v(33, -90) * mm});
            skLineSegment(sketch, "E94.MirrorCS", {"start": v(0, -90) * mm, "end": v(0, -120) * mm, "construction": true});
            skSolve(sketch);
        }
        {
            var Q0;
            {var subQ1=sQuery(id+"F16.wireOp",EDGE,"E79.0.1");Q0=makeQuery(id+"F16.imprint","IMPRINT",FACE,{"disambiguationData":[TD([[makeQuery(id+"F16.imprint","IMPRINT",EDGE,{"derivedFrom":subQ1}),1.0]])]});}
            var Q1;
            Q1=makeQuery(id+"F16.imprint","IMPRINT",FACE,{"disambiguationData":[TD([[makeQuery(id+"F16.imprint","IMPRINT",EDGE,{"derivedFrom":sQuery(id+"F16.wireOp",EDGE,"E80")}),-1.0]])]});
            var Q2;
            {var subQ0=sQuery(id+"F16.wireOp",EDGE,"E88.MirrorCS");Q2=makeQuery(id+"F16.imprint","IMPRINT",FACE,{"disambiguationData":[TD([[makeQuery(id+"F16.imprint","IMPRINT",EDGE,{"derivedFrom":subQ0}),1.0]])]});}
            var Q3;
            Q3=makeQuery(id+"F2.opExtrude","CAP_FACE",FACE,{"disambiguationData":[OSD([sQuery(id+"F0.wireOp",EDGE,"E12"),sQuery(id+"F0.wireOp",EDGE,"E13"),sQuery(id+"F0.wireOp",EDGE,"E14"),sQuery(id+"F0.wireOp",EDGE,"E15"),sQuery(id+"F0.wireOp",EDGE,"E17.filletArc"),sQuery(id+"F0.wireOp",EDGE,"E18.filletArc"),sQuery(id+"F0.wireOp",EDGE,"E19.filletArc"),sQuery(id+"F0.wireOp",EDGE,"E20.filletArc"),sQuery(id+"F0.wireOp",EDGE,"E25.0"),sQuery(id+"F0.wireOp",EDGE,"E25.1"),sQuery(id+"F0.wireOp",EDGE,"E25.2"),sQuery(id+"F0.wireOp",EDGE,"E25.3"),sQuery(id+"F0.wireOp",EDGE,"E25.4"),sQuery(id+"F0.wireOp",EDGE,"E25.5"),sQuery(id+"F0.wireOp",EDGE,"E25.6"),sQuery(id+"F0.wireOp",EDGE,"E25.7")])],"isStart":false});
            extrude(context, id + "F17", {"entities" : qUnion([Q0, Q1, Q2]), "endBound" : BoundingType.UP_TO_SURFACE, "depth" : 25 * mm, "endBoundEntityFace" : qUnion([Q3]), "offsetDistance" : 25 * mm});
        }
    });
